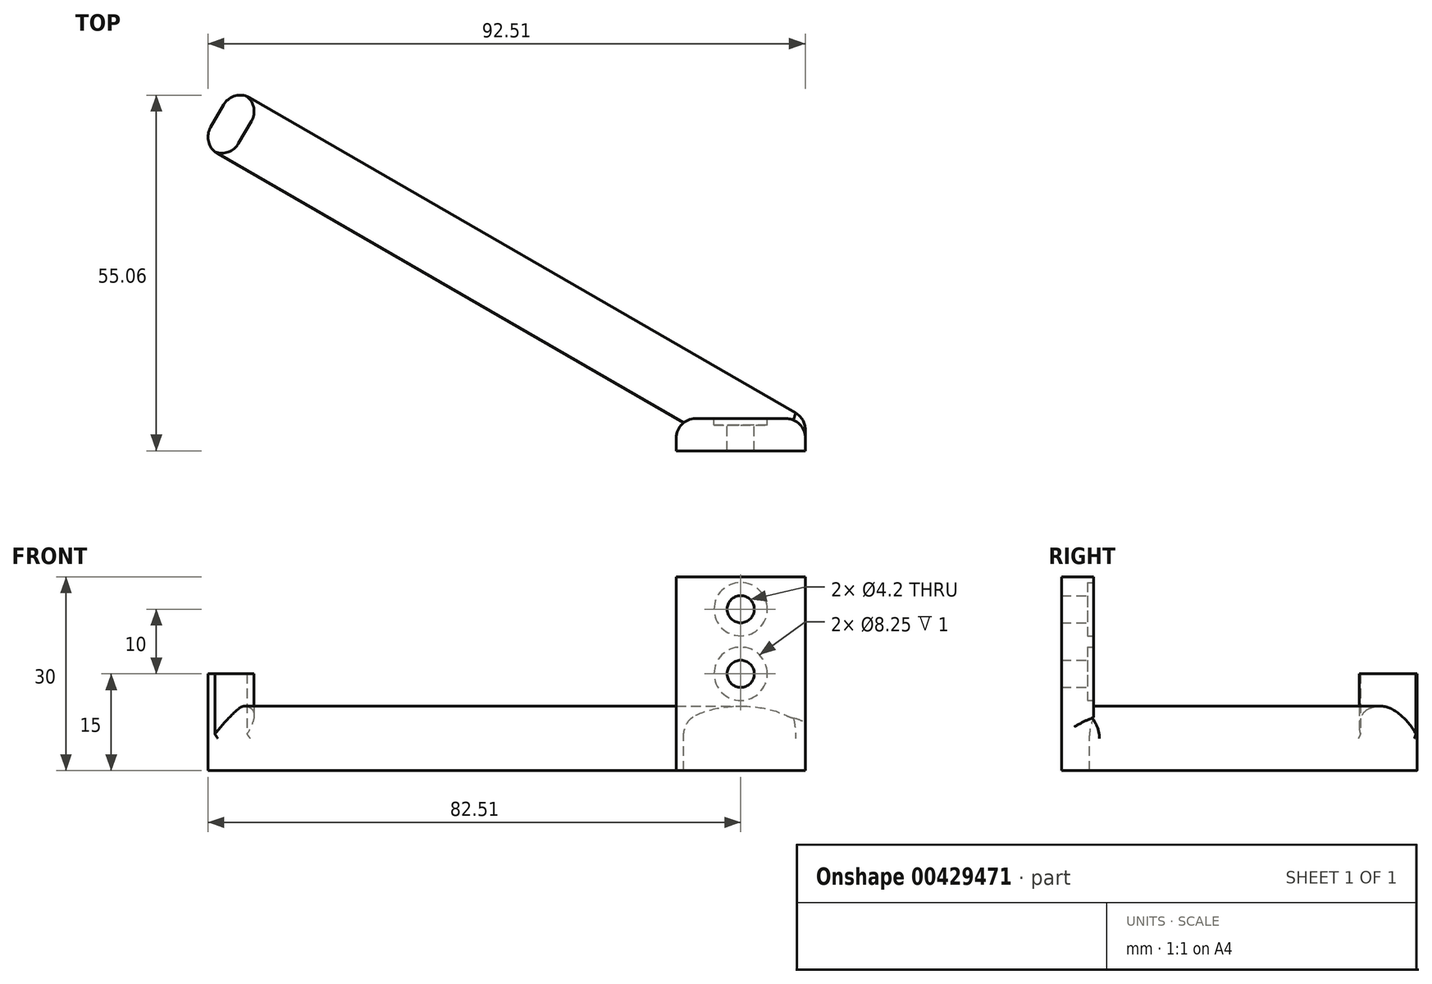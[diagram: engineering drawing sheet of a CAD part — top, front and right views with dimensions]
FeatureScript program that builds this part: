
annotation { "Feature Type Name" : "Feature", "Feature Type Description" : "" }
export const myFeature = defineFeature(function(context is Context, id is Id, definition is map)
    precondition{}
    {
        {
            assignVariable(context, id + "F0", {"name" : "wall_width", "anyValue" : 5});
        }
        {
            var Q0;
            Q0=qCreatedBy(makeId("Top.planeOp"),FACE);
            var sketch = newSketch(context, id + "F1", { "sketchPlane" : qUnion([Q0])});
            skLineSegment(sketch, "E0.bottom", {"start": v(0, 0) * mm, "end": v(20, 0) * mm});
            skLineSegment(sketch, "E0.top", {"start": v(0, -5) * mm, "end": v(20, -5) * mm});
            skLineSegment(sketch, "E0.left", {"start": v(0, 0) * mm, "end": v(0, -5) * mm});
            skLineSegment(sketch, "E0.right", {"start": v(20, 0) * mm, "end": v(20, -5) * mm});
            skLineSegment(sketch, "E1", {"start": v(0, 0) * mm, "end": v(-69.28, 40) * mm});
            skLineSegment(sketch, "E2", {"start": v(-69.28, 40) * mm, "end": v(-64.28, 48.66) * mm});
            skLineSegment(sketch, "E3", {"start": v(-64.28, 48.66) * mm, "end": v(20, 0) * mm});
            skSolve(sketch);
        }
        {
            var Q0;
            Q0=makeQuery(id+"F1.imprint","IMPRINT",FACE,{"disambiguationData":[TD([[makeQuery(id+"F1.imprint","IMPRINT",EDGE,{"derivedFrom":sQuery(id+"F1.wireOp",EDGE,"E0.bottom")}),-1.0]])]});
            extrude(context, id + "F2", {"entities" : qUnion([Q0]), "depth" : 30 * mm});
        }
        {
            var Q0;
            Q0=makeQuery(id+"F1.imprint","IMPRINT",FACE,{"disambiguationData":[TD([[makeQuery(id+"F1.imprint","IMPRINT",EDGE,{"derivedFrom":sQuery(id+"F1.wireOp",EDGE,"E0.bottom")}),1.0]])]});
            extrude(context, id + "F3", {"entities" : qUnion([Q0]), "operationType" : NewBodyOperationType.ADD, "depth" : 10 * mm});
        }
        {
            var Q0;
            Q0=makeQuery(id+"F3.opExtrude","CAP_EDGE",EDGE,{"disambiguationData":[OSD([sQuery(id+"F1.wireOp",EDGE,"E3")])],"isStart":false});
            var Q1;
            Q1=makeQuery(id+"F3.opExtrude","CAP_EDGE",EDGE,{"disambiguationData":[OSD([sQuery(id+"F1.wireOp",EDGE,"E1")])],"isStart":false});
            fillet(context, id + "F4", {"entities" : qUnion([Q0, Q1]), "radius" : 5 * mm, "tangentPropagation" : true, "allowEdgeOverflow" : false});
        }
        {
            var Q0;
            Q0=makeQuery(id+"F3.opExtrude","SWEPT_FACE",FACE,{"disambiguationData":[OSD([sQuery(id+"F1.wireOp",EDGE,"E2")])]});
            var sketch = newSketch(context, id + "F5", { "sketchPlane" : qUnion([Q0])});
            skLineSegment(sketch, "E4.bottom", {"start": v(-10, 0) * mm, "end": v(0, 0) * mm});
            skLineSegment(sketch, "E4.top", {"start": v(-10, 15) * mm, "end": v(0, 15) * mm});
            skLineSegment(sketch, "E4.left", {"start": v(-10, 0) * mm, "end": v(-10, 15) * mm});
            skLineSegment(sketch, "E4.right", {"start": v(0, 0) * mm, "end": v(0, 15) * mm});
            skSolve(sketch);
        }
        {
            var Q0;
            {var subQ4=sQuery(id+"F5.wireOp",EDGE,"E4.top");Q0=makeQuery(id+"F5.imprint","IMPRINT",FACE,{"disambiguationData":[TD([[makeQuery(id+"F5.imprint","IMPRINT",EDGE,{"derivedFrom":subQ4}),-1.0]])]});}
            var Q1;
            {var subQ4=sQuery(id+"F5.wireOp",EDGE,"E4.bottom");Q1=makeQuery(id+"F5.imprint","IMPRINT",FACE,{"disambiguationData":[TD([[makeQuery(id+"F5.imprint","IMPRINT",EDGE,{"derivedFrom":subQ4}),-1.0]])]});}
            extrude(context, id + "F6", {"entities" : qUnion([Q0, Q1]), "operationType" : NewBodyOperationType.ADD, "depth" : getVariable(context, 'wall_width') * mm});
        }
        {
            var Q0;
            Q0=makeQuery(id+"F6.opExtrude","CAP_EDGE",EDGE,{"disambiguationData":[OSD([sQuery(id+"F5.wireOp",EDGE,"E4.right")])],"isStart":true});
            var Q1;
            Q1=makeQuery(id+"F6.opExtrude","CAP_EDGE",EDGE,{"disambiguationData":[OSD([sQuery(id+"F5.wireOp",EDGE,"E4.left")])],"isStart":true});
            var Q2;
            Q2=makeQuery(id+"F6.opExtrude","CAP_EDGE",EDGE,{"disambiguationData":[OSD([sQuery(id+"F5.wireOp",EDGE,"E4.right")])],"isStart":false});
            var Q3;
            Q3=makeQuery(id+"F6.opExtrude","CAP_EDGE",EDGE,{"disambiguationData":[OSD([sQuery(id+"F5.wireOp",EDGE,"E4.left")])],"isStart":false});
            var Q4;
            {var subQ0=sQuery(id+"F1.wireOp",EDGE,"E3");var subQ1=sQuery(id+"F1.wireOp",EDGE,"E0.right");var subQ2=sQuery(id+"F1.wireOp",EDGE,"E0.bottom");var subQ3=makeQuery(id+"F2.opExtrude","SWEPT_EDGE",EDGE,{"disambiguationData":[OSD([subQ2,subQ1,subQ0])]});Q4=makeQuery(id+"F4.opFillet","MERGE",EDGE,{"derivedFrom":[makeQuery(id+"F3.boolean.opBoolean","MERGE",EDGE,{"derivedFrom":[subQ3,makeQuery(id+"F3.opExtrude","SWEPT_EDGE",EDGE,{"disambiguationData":[OSD([subQ2,subQ1,subQ0])]})]}),makeQuery(id+"F3.boolean.opBoolean","SPLIT",EDGE,{"derivedFrom":subQ3})]});}
            var Q5;
            Q5=makeQuery(id+"F3.boolean.opBoolean","SPLIT",EDGE,{"derivedFrom":makeQuery(id+"F2.opExtrude","SWEPT_EDGE",EDGE,{"disambiguationData":[OSD([sQuery(id+"F1.wireOp",EDGE,"E0.bottom"),sQuery(id+"F1.wireOp",EDGE,"E0.left"),sQuery(id+"F1.wireOp",EDGE,"E1")])]})});
            fillet(context, id + "F7", {"entities" : qUnion([Q0, Q1, Q2, Q3, Q4, Q5]), "radius" : 3 * mm, "tangentPropagation" : true, "allowEdgeOverflow" : false});
        }
        {
            var Q0;
            Q0=makeQuery(id+"F2.opExtrude","SWEPT_FACE",FACE,{"disambiguationData":[OSD([sQuery(id+"F1.wireOp",EDGE,"E0.bottom")])]});
            var sketch = newSketch(context, id + "F8", { "sketchPlane" : qUnion([Q0])});
            skPoint(sketch, "E5", {"position": v(-10, 25) * mm});
            skPoint(sketch, "E5.positionSnap0", {"position": v(-10, 30) * mm});
            skPoint(sketch, "E6", {"position": v(-10, 15) * mm});
            skPoint(sketch, "E7", {"position": v(-10, 10) * mm});
            skLineSegment(sketch, "E8", {"start": v(-10, 30) * mm, "end": v(-10, 25) * mm, "construction": true});
            skLineSegment(sketch, "E9", {"start": v(-10, 25) * mm, "end": v(-10, 15) * mm, "construction": true});
            skLineSegment(sketch, "E10", {"start": v(-10, 15) * mm, "end": v(-10, 10) * mm, "construction": true});
            skSolve(sketch);
        }
        {
            var Q0;
            Q0=sQuery(id+"F8.wireOp",VERTEX,"E5");
            var Q1;
            Q1=sQuery(id+"F8.wireOp",VERTEX,"E6");
            var Q2;
            Q2=makeQuery(id+"F2.opExtrude","SWEPT_BODY",BODY,{"disambiguationData":[OSD([sQuery(id+"F1.wireOp",EDGE,"E0.bottom"),sQuery(id+"F1.wireOp",EDGE,"E0.top"),sQuery(id+"F1.wireOp",EDGE,"E0.left"),sQuery(id+"F1.wireOp",EDGE,"E0.right")])]});
            hole(context, id + "F9", {"style" : HoleStyle.C_BORE, "endStyle" : HoleEndStyle.THROUGH, "holeDiameter" : 4.2 * mm, "cBoreDiameter" : 8.25 * mm, "cBoreDepth" : 1 * mm, "isTappedThrough" : true, "tappedDepth" : 12 * mm, "tapClearance" : 3, "locations" : qUnion([Q0, Q1]), "scope" : qUnion([Q2])});
        }
    });
